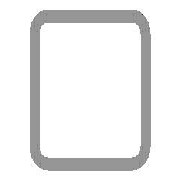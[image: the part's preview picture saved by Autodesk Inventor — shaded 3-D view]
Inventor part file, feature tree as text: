
AUTODESK INVENTOR PART (.ipt)
format: ipt  version: 2025.1 (Build 291241020, 241B)  size: 144,384 bytes
history: native  units: mm (DEFAULTED — no unit token found)
features: other x4, sketch x1, plane x1
ambient origin geometry x8: Origin, YZ Plane, XZ Plane, XY Plane, X Axis, Y Axis, Z Axis, Center Point
bodies: Solid1 (feature_tree), Body (feature_tree)
feature tree (6):
  parser-record x1  (decoder bookkeeping rows leaked as tree rows — omitted from the tree; the rows remain in map.json)
  other  "Driven Length"
  other  "Start plane"
  other  "End plane"
  sketch  "Sketch3"  dims[d3=7000.0mm d4=0.0mm d7=6.0mm d9=100.0mm d11=100.0mm d12=3.0mm d13=-0.0mm d14=7000.0mm d15=50.0mm d16=50.0mm d17=90.0deg d18=7000.0mm]
  plane  "Work Plane3"
